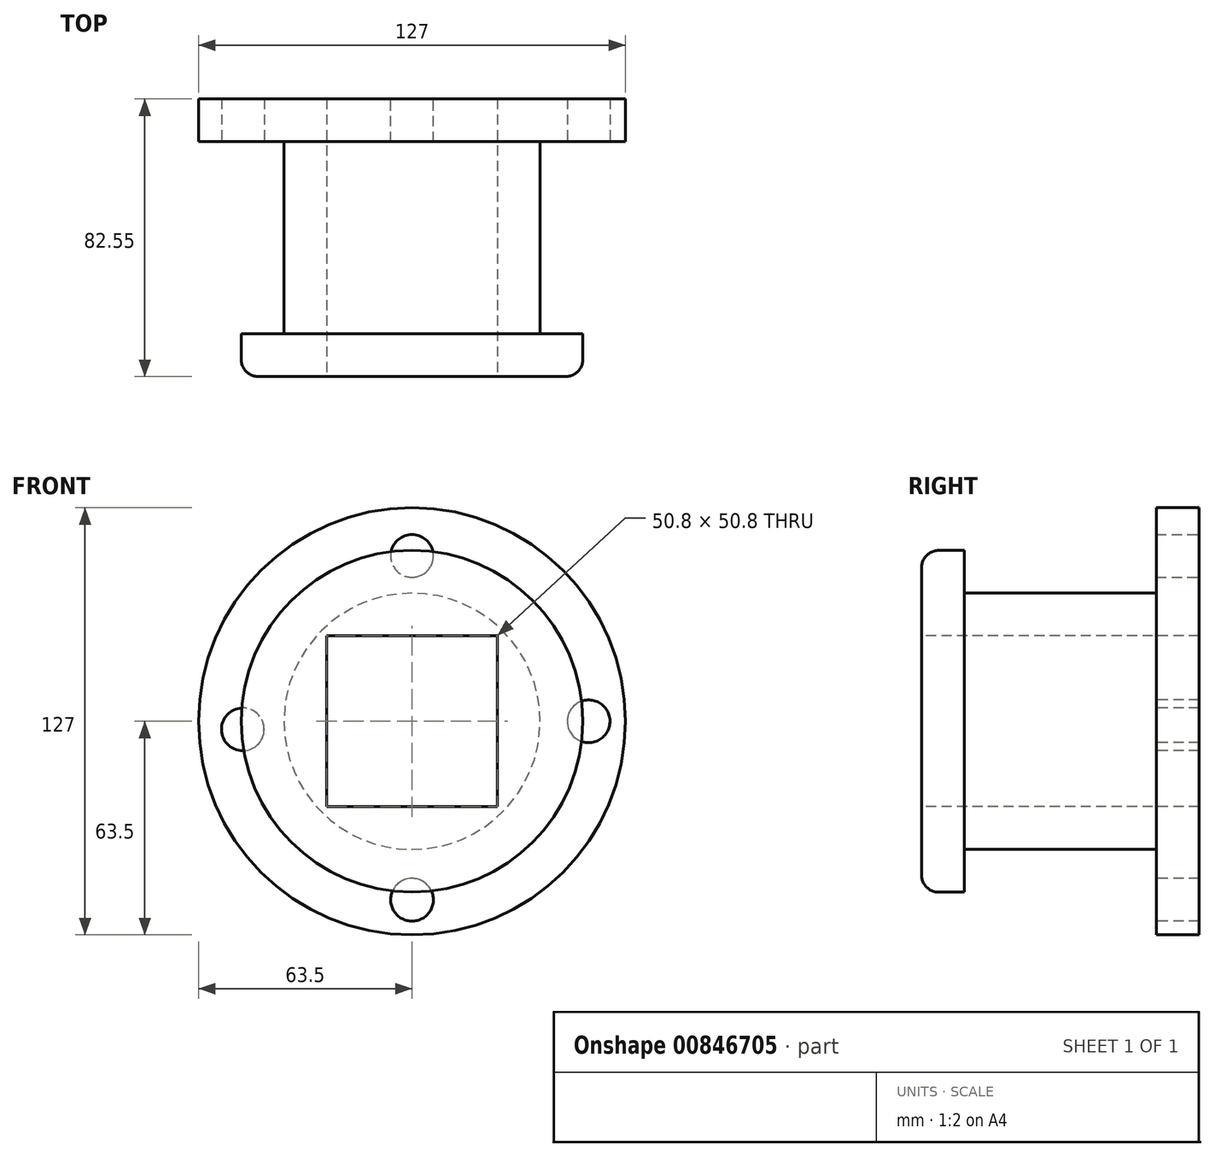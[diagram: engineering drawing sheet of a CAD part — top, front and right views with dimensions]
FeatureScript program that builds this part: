
annotation { "Feature Type Name" : "Feature", "Feature Type Description" : "" }
export const myFeature = defineFeature(function(context is Context, id is Id, definition is map)
    precondition{}
    {
        {
            var Q0;
            Q0=qCreatedBy(makeId("Front.planeOp"),FACE);
            var sketch = newSketch(context, id + "F0", { "sketchPlane" : qUnion([Q0])});
            skCircle(sketch, "E0", {"center": v(0, 0) * mm, "radius": 63.5 * mm});
            skLineSegment(sketch, "E1", {"start": v(-42.95, 46.77) * mm, "end": v(42.95, -46.77) * mm});
            skSolve(sketch);
        }
        {
            var Q0;
            Q0 = qSketchRegion(id + "F0", true);
            extrude(context, id + "F1", {"entities" : qUnion([Q0]), "depth" : 12.7 * mm, "offsetDistance" : 25.4 * mm});
        }
        {
            var Q0;
            Q0=makeQuery(id+"F1.opExtrude","CAP_FACE",FACE,{"disambiguationData":[OSD([sQuery(id+"F0.wireOp",EDGE,"E0")])],"isStart":false});
            var sketch = newSketch(context, id + "F2", { "sketchPlane" : qUnion([Q0])});
            skCircle(sketch, "E2", {"center": v(0, 0) * mm, "radius": 38.1 * mm});
            skSolve(sketch);
        }
        {
            var Q0;
            Q0=makeQuery(id+"F2.imprint","IMPRINT",FACE,{"disambiguationData":[TD([[makeQuery(id+"F2.imprint","IMPRINT",EDGE,{"derivedFrom":sQuery(id+"F2.wireOp",EDGE,"E2")}),1.0]])]});
            extrude(context, id + "F3", {"entities" : qUnion([Q0]), "operationType" : NewBodyOperationType.ADD, "depth" : 57.15 * mm, "offsetDistance" : 25.4 * mm});
        }
        {
            var Q0;
            Q0=makeQuery(id+"F3.opExtrude","CAP_FACE",FACE,{"disambiguationData":[OSD([sQuery(id+"F2.wireOp",EDGE,"E2")])],"isStart":false});
            var sketch = newSketch(context, id + "F4", { "sketchPlane" : qUnion([Q0])});
            skCircle(sketch, "E3", {"center": v(0, 0) * mm, "radius": 50.8 * mm});
            skSolve(sketch);
        }
        {
            var Q0;
            Q0 = qSketchRegion(id + "F4", true);
            extrude(context, id + "F5", {"entities" : qUnion([Q0]), "operationType" : NewBodyOperationType.ADD, "depth" : 12.7 * mm, "offsetDistance" : 25.4 * mm});
        }
        {
            var Q0;
            Q0=makeQuery(id+"F5.opExtrude","CAP_EDGE",EDGE,{"disambiguationData":[OSD([sQuery(id+"F4.wireOp",EDGE,"E3")])],"isStart":false});
            fillet(context, id + "F6", {"entities" : qUnion([Q0]), "radius" : 5.08 * mm, "tangentPropagation" : true, "allowEdgeOverflow" : false});
        }
        {
            var Q0;
            Q0=makeQuery(id+"F5.opExtrude","CAP_FACE",FACE,{"disambiguationData":[OSD([sQuery(id+"F4.wireOp",EDGE,"E3")])],"isStart":false});
            var sketch = newSketch(context, id + "F7", { "sketchPlane" : qUnion([Q0])});
            skLineSegment(sketch, "E4.bottom", {"start": v(-25.4, 25.4) * mm, "end": v(25.4, 25.4) * mm});
            skLineSegment(sketch, "E4.top", {"start": v(-25.4, -25.4) * mm, "end": v(25.4, -25.4) * mm});
            skLineSegment(sketch, "E4.left", {"start": v(-25.4, 25.4) * mm, "end": v(-25.4, -25.4) * mm});
            skLineSegment(sketch, "E4.right", {"start": v(25.4, 25.4) * mm, "end": v(25.4, -25.4) * mm});
            skPoint(sketch, "E4.middle", {"position": v(0, 0) * mm});
            skSolve(sketch);
        }
        {
            var Q0;
            Q0=makeQuery(id+"F7.imprint","IMPRINT",FACE,{"disambiguationData":[TD([[makeQuery(id+"F7.imprint","IMPRINT",EDGE,{"derivedFrom":sQuery(id+"F7.wireOp",EDGE,"E4.bottom")}),-1.0]])]});
            extrude(context, id + "F8", {"entities" : qUnion([Q0]), "operationType" : NewBodyOperationType.REMOVE, "oppositeDirection" : true, "depth" : 101.6 * mm, "offsetDistance" : 25.4 * mm});
        }
        {
            var Q0;
            Q0=makeQuery(id+"F1.opExtrude","CAP_FACE",FACE,{"disambiguationData":[OSD([sQuery(id+"F0.wireOp",EDGE,"E0")])],"isStart":false});
            var sketch = newSketch(context, id + "F9", { "sketchPlane" : qUnion([Q0])});
            skSolve(sketch);
        }
        {
            var Q0;
            Q0=makeQuery(id+"F9.imprint","IMPRINT",FACE,{"disambiguationData":[TD([[makeQuery(id+"F9.imprint","IMPRINT",EDGE,{"derivedFrom":makeQuery(id+"F1.opExtrude","CAP_EDGE",EDGE,{"disambiguationData":[OSD([sQuery(id+"F0.wireOp",EDGE,"E0")])],"isStart":false})}),1.0]])]});
            var sketch = newSketch(context, id + "F10", { "sketchPlane" : qUnion([Q0])});
            skCircle(sketch, "E5", {"center": v(0, -53.05) * mm, "radius": 6.35 * mm});
            skSolve(sketch);
        }
        {
            var Q0;
            Q0=makeQuery(id+"F9.imprint","IMPRINT",FACE,{"disambiguationData":[TD([[makeQuery(id+"F9.imprint","IMPRINT",EDGE,{"derivedFrom":makeQuery(id+"F1.opExtrude","CAP_EDGE",EDGE,{"disambiguationData":[OSD([sQuery(id+"F0.wireOp",EDGE,"E0")])],"isStart":false})}),1.0]])]});
            var sketch = newSketch(context, id + "F11", { "sketchPlane" : qUnion([Q0])});
            skCircle(sketch, "E6", {"center": v(-50.35, -2.38) * mm, "radius": 6.35 * mm});
            skSolve(sketch);
        }
        {
            var Q0;
            Q0=makeQuery(id+"F9.imprint","IMPRINT",FACE,{"disambiguationData":[TD([[makeQuery(id+"F9.imprint","IMPRINT",EDGE,{"derivedFrom":makeQuery(id+"F1.opExtrude","CAP_EDGE",EDGE,{"disambiguationData":[OSD([sQuery(id+"F0.wireOp",EDGE,"E0")])],"isStart":false})}),1.0]])]});
            var sketch = newSketch(context, id + "F12", { "sketchPlane" : qUnion([Q0])});
            skCircle(sketch, "E7", {"center": v(52.55, 0) * mm, "radius": 6.35 * mm});
            skSolve(sketch);
        }
        {
            var Q0;
            Q0=makeQuery(id+"F1.opExtrude","CAP_FACE",FACE,{"disambiguationData":[OSD([sQuery(id+"F0.wireOp",EDGE,"E0")])],"isStart":true});
            var sketch = newSketch(context, id + "F13", { "sketchPlane" : qUnion([Q0])});
            skCircle(sketch, "E8", {"center": v(0, 49.17) * mm, "radius": 6.35 * mm});
            skSolve(sketch);
        }
        {
            var Q0;
            Q0=makeQuery(id+"F13.imprint","IMPRINT",FACE,{"disambiguationData":[TD([[makeQuery(id+"F13.imprint","IMPRINT",EDGE,{"derivedFrom":sQuery(id+"F13.wireOp",EDGE,"E8")}),1.0]])]});
            extrude(context, id + "F14", {"entities" : qUnion([Q0]), "operationType" : NewBodyOperationType.REMOVE, "oppositeDirection" : true, "depth" : 50.8 * mm, "offsetDistance" : 25.4 * mm});
        }
        {
            var Q0;
            Q0=makeQuery(id+"F11.imprint","IMPRINT",FACE,{"disambiguationData":[TD([[makeQuery(id+"F11.imprint","IMPRINT",EDGE,{"derivedFrom":sQuery(id+"F11.wireOp",EDGE,"E6")}),1.0]])]});
            extrude(context, id + "F15", {"entities" : qUnion([Q0]), "operationType" : NewBodyOperationType.REMOVE, "oppositeDirection" : true, "depth" : 50.8 * mm, "offsetDistance" : 25.4 * mm});
        }
        {
            var Q0;
            Q0=makeQuery(id+"F10.imprint","IMPRINT",FACE,{"disambiguationData":[TD([[makeQuery(id+"F10.imprint","IMPRINT",EDGE,{"derivedFrom":sQuery(id+"F10.wireOp",EDGE,"E5")}),1.0]])]});
            var sketch = newSketch(context, id + "F16", { "sketchPlane" : qUnion([Q0])});
            skSolve(sketch);
        }
        {
            var Q0;
            Q0 = qSketchRegion(id + "F16", true);
            var Q1;
            Q1=makeQuery(id+"F10.imprint","IMPRINT",FACE,{"disambiguationData":[TD([[makeQuery(id+"F10.imprint","IMPRINT",EDGE,{"derivedFrom":sQuery(id+"F10.wireOp",EDGE,"E5")}),1.0]])]});
            extrude(context, id + "F17", {"entities" : qUnion([Q0, Q1]), "operationType" : NewBodyOperationType.REMOVE, "oppositeDirection" : true, "depth" : 50.8 * mm, "offsetDistance" : 25.4 * mm});
        }
        {
            var Q0;
            Q0=makeQuery(id+"F12.imprint","IMPRINT",FACE,{"disambiguationData":[TD([[makeQuery(id+"F12.imprint","IMPRINT",EDGE,{"derivedFrom":sQuery(id+"F12.wireOp",EDGE,"E7")}),1.0]])]});
            extrude(context, id + "F18", {"entities" : qUnion([Q0]), "operationType" : NewBodyOperationType.REMOVE, "oppositeDirection" : true, "depth" : 50.8 * mm, "offsetDistance" : 25.4 * mm});
        }
    });
